# Revit family: P560031-031
name_source: partatom
category: Lighting Fixtures
revit_build: Autodesk Revit 2014 (Build: 20130308_1515(x64)
units: mm (PartAtom-declared; Revit-internal decimal feet)

## types (1)
- P560031-031
    Apparent Load = 100 VA
    Assembly Code = D5020200
    Color Filter = 16777215
    Connector Description = Lighting Connector
    Default Elevation = 48 "
    Description = Creighton Collection One-Light Small Wall-Lantern
    Dimming Lamp Color Temperature Shift = <None>
    Features = Black finish.
Cottage-inspired outdoor lantern.
Features a tapered cage design.
Clear water glass panels.
Linear details enhance mechanical detailing of fixture.
    Fixture distribution = Direct
    Glass = Paint - Hubbell - White Texture
    Gold = Hubbell - Gold
    Housing Material = Paint - Hubbell - Textured Camera Black
    Lamp = Incandescent A-19
    Load Classification = Lighting
    Manufacturer = Progress Lighting
    Model = P560031-031
    Photometric Web File = generic
    Power Factor = 1
    Product Documentation Link = https://hubbellcdn.com
    Product Link = https://www.hubbell.com
    Steel = Paint - Hubbell - Stainless Stell
    Support = Paint - Hubbell - Stainless Stell
    Tilt Angle = 60.00°
    URL = https://www.hubbell.com
    Voltage = 120 V
    Warranty = 1 year Warranty
    Wattage Comments = 100W
    Watts = 100 W

## geometry (parser evidence)
native form markers: Sweep x2
no freeform markers — native parametric forms only
